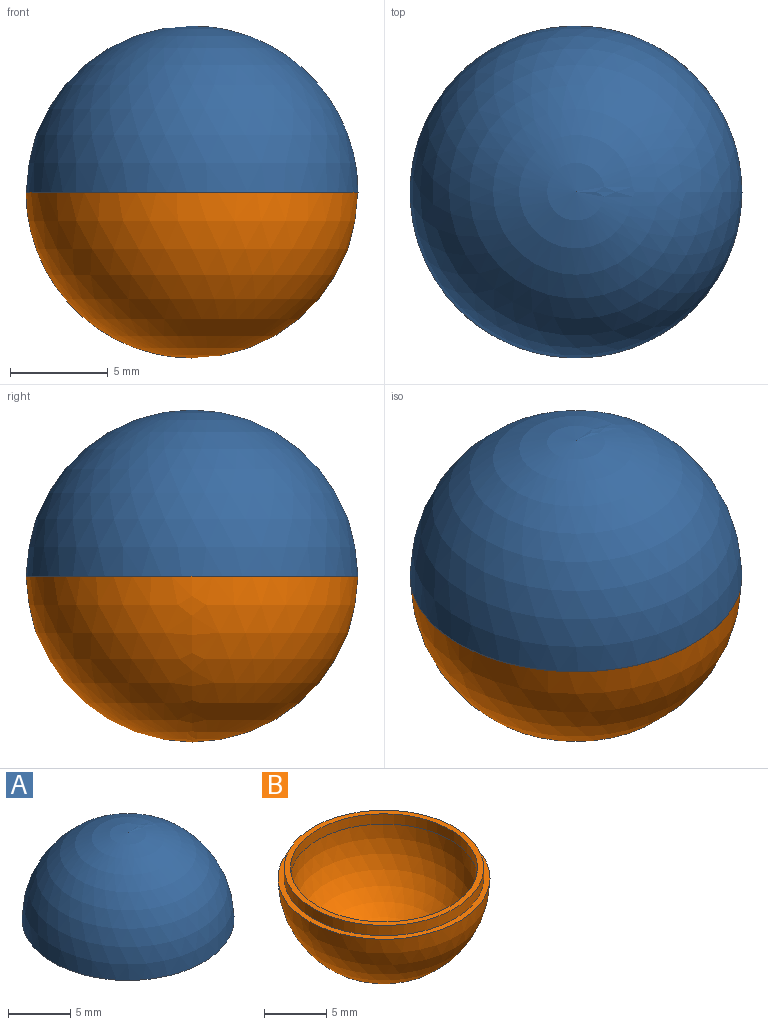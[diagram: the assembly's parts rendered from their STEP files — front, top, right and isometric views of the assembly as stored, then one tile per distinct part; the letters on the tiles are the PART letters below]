
ASSEMBLY  parts=2 mates=1
PART A: 5 faces, bbox 17x17x8.5 mm
  f0: sphere r=8.5mm, area 454mm2, adj f1
  f1: plane 17x17mm, normal (0,0,-1), area 25.9mm2, adj f0,f2
  f2: cylinder r=8mm len=16mm, axis (0,0,1), area 50.3mm2, adj f1,f3
  f3: plane 16x16mm, normal (0,0,-1), area 27.5mm2, adj f2,f4
  f4: sphere r=7.5mm, area 306.3mm2, adj f3
PART B: 6 faces, bbox 17x17x9.5 mm
  f0: cylinder r=8mm len=16mm, axis (0,0,-1), area 50.3mm2, adj f1,f5
  f1: plane 17x17mm, normal (0,0,1), area 25.9mm2, adj f0,f2
  f2: sphere r=8.5mm, area 454mm2, adj f1
  f3: sphere r=7.5mm, area 353.4mm2, adj f4
  f4: cylinder r=7.5mm len=15mm, axis (0,0,-1), area 47.1mm2, adj f3,f5
  f5: plane 16x16mm, normal (0,0,1), area 24.3mm2, adj f0,f4
PLACE A t=(0,0,-15)mm
PLACE B at identity fixed
MATE fastened B.f0 <-> A.f2  axis (0,0,1) through (0,0,0)mm
